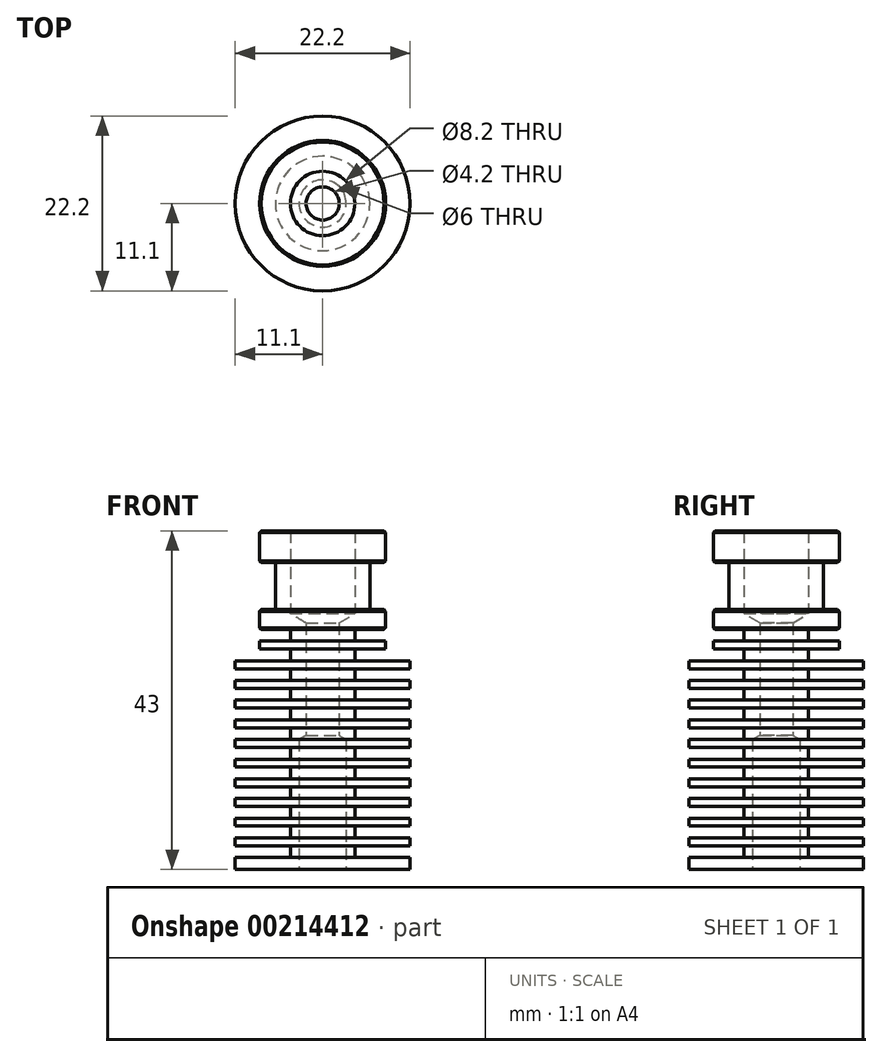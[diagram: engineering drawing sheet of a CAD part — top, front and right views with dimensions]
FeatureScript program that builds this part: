
annotation { "Feature Type Name" : "Feature", "Feature Type Description" : "" }
export const myFeature = defineFeature(function(context is Context, id is Id, definition is map)
    precondition{}
    {
        {
            var Q0;
            Q0=qCreatedBy(makeId("Front.planeOp"),FACE);
            var sketch = newSketch(context, id + "F0", { "sketchPlane" : qUnion([Q0])});
            skLineSegment(sketch, "E0", {"start": v(0, 0) * mm, "end": v(0, 43) * mm, "construction": true});
            skLineSegment(sketch, "E1", {"start": v(4.1, 43) * mm, "end": v(8, 43) * mm});
            skLineSegment(sketch, "E2", {"start": v(8, 43) * mm, "end": v(8, 39) * mm});
            skLineSegment(sketch, "E3", {"start": v(8, 39) * mm, "end": v(6, 39) * mm});
            skLineSegment(sketch, "E4", {"start": v(6, 39) * mm, "end": v(6, 33) * mm});
            skLineSegment(sketch, "E5", {"start": v(6, 33) * mm, "end": v(8, 33) * mm});
            skLineSegment(sketch, "E6", {"start": v(8, 33) * mm, "end": v(8, 30.5) * mm});
            skLineSegment(sketch, "E7", {"start": v(8, 30.5) * mm, "end": v(4.1, 30.5) * mm});
            skLineSegment(sketch, "E8", {"start": v(4.1, 30.5) * mm, "end": v(4.1, 29) * mm});
            skLineSegment(sketch, "E9", {"start": v(4.1, 29) * mm, "end": v(8, 29) * mm});
            skLineSegment(sketch, "E10", {"start": v(8, 29) * mm, "end": v(8, 28) * mm});
            skLineSegment(sketch, "E11", {"start": v(8, 28) * mm, "end": v(4.1, 28) * mm});
            skLineSegment(sketch, "E12", {"start": v(4.1, 28) * mm, "end": v(4.1, 26.5) * mm});
            skLineSegment(sketch, "E13", {"start": v(4.1, 26.5) * mm, "end": v(11.1, 26.5) * mm});
            skLineSegment(sketch, "E14", {"start": v(11.1, 26.5) * mm, "end": v(11.1, 25.5) * mm});
            skLineSegment(sketch, "E15", {"start": v(11.1, 25.5) * mm, "end": v(4.1, 25.5) * mm});
            skLineSegment(sketch, "E16", {"start": v(4.1, 25.5) * mm, "end": v(4.1, 24) * mm});
            skLineSegment(sketch, "E17", {"start": v(4.1, 24) * mm, "end": v(11.1, 24) * mm});
            skLineSegment(sketch, "E18", {"start": v(11.1, 24) * mm, "end": v(11.1, 23) * mm});
            skLineSegment(sketch, "E19", {"start": v(11.1, 23) * mm, "end": v(4.1, 23) * mm});
            skLineSegment(sketch, "E20", {"start": v(4.1, 23) * mm, "end": v(4.1, 21.5) * mm});
            skLineSegment(sketch, "E21", {"start": v(4.1, 21.5) * mm, "end": v(11.1, 21.5) * mm});
            skLineSegment(sketch, "E22", {"start": v(11.1, 21.5) * mm, "end": v(11.1, 20.5) * mm});
            skLineSegment(sketch, "E23", {"start": v(11.1, 20.5) * mm, "end": v(4.1, 20.5) * mm});
            skLineSegment(sketch, "E24", {"start": v(4.1, 20.5) * mm, "end": v(4.1, 19) * mm});
            skLineSegment(sketch, "E25", {"start": v(4.1, 19) * mm, "end": v(11.1, 19) * mm});
            skLineSegment(sketch, "E26", {"start": v(11.1, 19) * mm, "end": v(11.1, 18) * mm});
            skLineSegment(sketch, "E27", {"start": v(11.1, 18) * mm, "end": v(4.1, 18) * mm});
            skLineSegment(sketch, "E28", {"start": v(4.1, 18) * mm, "end": v(4.1, 16.5) * mm});
            skLineSegment(sketch, "E29", {"start": v(4.1, 16.5) * mm, "end": v(11.1, 16.5) * mm});
            skLineSegment(sketch, "E30", {"start": v(11.1, 16.5) * mm, "end": v(11.1, 15.5) * mm});
            skLineSegment(sketch, "E31", {"start": v(11.1, 15.5) * mm, "end": v(4.1, 15.5) * mm});
            skLineSegment(sketch, "E32", {"start": v(4.1, 15.5) * mm, "end": v(4.1, 14) * mm});
            skLineSegment(sketch, "E33", {"start": v(4.1, 14) * mm, "end": v(11.1, 14) * mm});
            skLineSegment(sketch, "E34", {"start": v(11.1, 14) * mm, "end": v(11.1, 13) * mm});
            skLineSegment(sketch, "E35", {"start": v(11.1, 13) * mm, "end": v(4.1, 13) * mm});
            skLineSegment(sketch, "E36", {"start": v(4.1, 13) * mm, "end": v(4.1, 11.5) * mm});
            skLineSegment(sketch, "E37", {"start": v(4.1, 11.5) * mm, "end": v(11.1, 11.5) * mm});
            skLineSegment(sketch, "E38", {"start": v(11.1, 11.5) * mm, "end": v(11.1, 10.5) * mm});
            skLineSegment(sketch, "E39", {"start": v(11.1, 10.5) * mm, "end": v(4.1, 10.5) * mm});
            skLineSegment(sketch, "E40", {"start": v(4.1, 10.5) * mm, "end": v(4.1, 9) * mm});
            skLineSegment(sketch, "E41", {"start": v(4.1, 9) * mm, "end": v(11.1, 9) * mm});
            skLineSegment(sketch, "E42", {"start": v(11.1, 9) * mm, "end": v(11.1, 8) * mm});
            skLineSegment(sketch, "E43", {"start": v(11.1, 8) * mm, "end": v(4.1, 8) * mm});
            skLineSegment(sketch, "E44", {"start": v(4.1, 8) * mm, "end": v(4.1, 6.5) * mm});
            skLineSegment(sketch, "E45", {"start": v(4.1, 6.5) * mm, "end": v(11.1, 6.5) * mm});
            skLineSegment(sketch, "E46", {"start": v(11.1, 6.5) * mm, "end": v(11.1, 5.5) * mm});
            skLineSegment(sketch, "E47", {"start": v(11.1, 5.5) * mm, "end": v(4.1, 5.5) * mm});
            skLineSegment(sketch, "E48", {"start": v(4.1, 5.5) * mm, "end": v(4.1, 4) * mm});
            skLineSegment(sketch, "E49", {"start": v(4.1, 4) * mm, "end": v(11.1, 4) * mm});
            skLineSegment(sketch, "E50", {"start": v(11.1, 4) * mm, "end": v(11.1, 3) * mm});
            skLineSegment(sketch, "E51", {"start": v(11.1, 3) * mm, "end": v(4.1, 3) * mm});
            skLineSegment(sketch, "E52", {"start": v(4.1, 3) * mm, "end": v(4.1, 1.5) * mm});
            skLineSegment(sketch, "E53", {"start": v(4.1, 1.5) * mm, "end": v(11.1, 1.5) * mm});
            skLineSegment(sketch, "E54", {"start": v(11.1, 1.5) * mm, "end": v(11.1, 0) * mm});
            skLineSegment(sketch, "E55", {"start": v(11.1, 0) * mm, "end": v(3, 0) * mm});
            skLineSegment(sketch, "E56", {"start": v(4.1, 43) * mm, "end": v(4.1, 32.5) * mm});
            skLineSegment(sketch, "E57", {"start": v(4.1, 32.5) * mm, "end": v(2.1, 31.3) * mm});
            skLineSegment(sketch, "E58", {"start": v(2.1, 31.3) * mm, "end": v(2.1, 17.04) * mm});
            skLineSegment(sketch, "E59", {"start": v(2.1, 17.04) * mm, "end": v(3, 16.5) * mm});
            skLineSegment(sketch, "E60", {"start": v(3, 16.5) * mm, "end": v(3, 0) * mm});
            skSolve(sketch);
        }
        {
            var Q0;
            Q0 = qSketchRegion(id + "F0", true);
            var Q1;
            Q1=sQuery(id+"F0.wireOp",EDGE,"E0");
            revolve(context, id + "F1", {"entities" : qUnion([Q0]), "axis" : qUnion([Q1]), "revolveType" : RevolveType.FULL});
        }
        {
            var Q0;
            Q0=makeQuery(id+"F1.opRevolve","SWEPT_EDGE",EDGE,{"disambiguationData":[OSD([sQuery(id+"F0.wireOp",EDGE,"E6"),sQuery(id+"F0.wireOp",EDGE,"E7")])]});
            var Q1;
            Q1=makeQuery(id+"F1.opRevolve","SWEPT_EDGE",EDGE,{"disambiguationData":[OSD([sQuery(id+"F0.wireOp",EDGE,"E5"),sQuery(id+"F0.wireOp",EDGE,"E6")])]});
            var Q2;
            Q2=makeQuery(id+"F1.opRevolve","SWEPT_EDGE",EDGE,{"disambiguationData":[OSD([sQuery(id+"F0.wireOp",EDGE,"E2"),sQuery(id+"F0.wireOp",EDGE,"E3")])]});
            var Q3;
            Q3=makeQuery(id+"F1.opRevolve","SWEPT_EDGE",EDGE,{"disambiguationData":[OSD([sQuery(id+"F0.wireOp",EDGE,"E1"),sQuery(id+"F0.wireOp",EDGE,"E2")])]});
            chamfer(context, id + "F2", {"entities" : qUnion([Q0, Q1, Q2, Q3]), "width" : 0.2 * mm, "tangentPropagation" : true});
        }
    });
